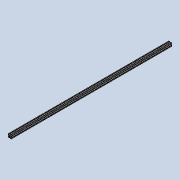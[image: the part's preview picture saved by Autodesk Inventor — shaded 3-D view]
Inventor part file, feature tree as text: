
AUTODESK INVENTOR PART (.ipt)
format: ipt  version: 2022 (Build 260153000, 153)  size: 198,656 bytes
history: native  units: in
note: dims shown in document units (in); Inventor stores cm internally (conversion verified against a paired STEP export)
features: mirror x1
ambient origin geometry x8: Origin, YZ Plane, XZ Plane, XY Plane, X Axis, Y Axis, Z Axis, Center Point
bodies: Solid1 (feature_tree)
feature tree (1):
  mirror  "Mirror2"
